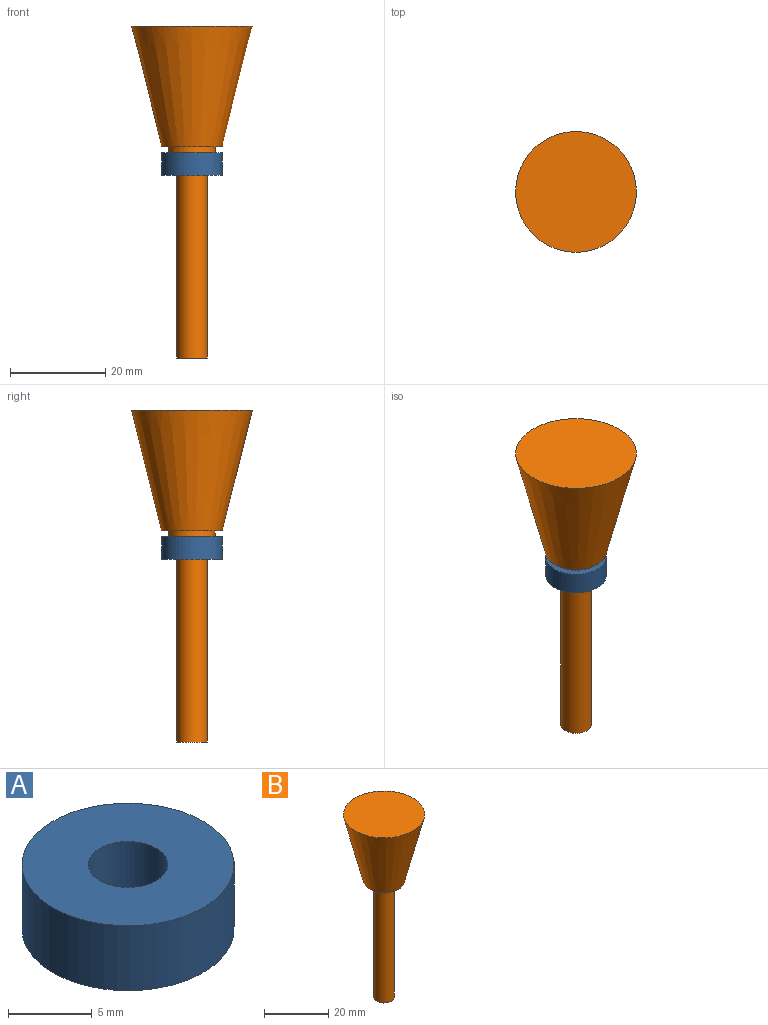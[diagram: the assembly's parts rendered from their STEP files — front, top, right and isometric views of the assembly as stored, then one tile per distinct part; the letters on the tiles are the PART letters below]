
ASSEMBLY  parts=2 mates=1
PART A: 4 faces, bbox 12.7x12.7x4.8 mm
  f0: cylinder r=2.38mm len=4.76mm, axis (0,0,-1), area 71.3mm2, adj f2,f3
  f1: cylinder r=6.35mm len=12.7mm, axis (0,0,-1), area 190mm2, adj f2,f3
  f2: plane 12.7x12.7mm, normal (0,0,1), area 108.9mm2, adj f0,f1
  f3: plane 12.7x12.7mm, normal (0,0,-1), area 108.9mm2, adj f0,f1
PART B: 7 faces, bbox 34.4x34.4x69.9 mm
  f0: torus R=42.94mm, axis (0,0,1), area 38.7mm2, adj f3,f4
  f1: plane 25.4x25.4mm, normal (0,0,1), area 506.7mm2, adj f2
  f2: cone r=12.7mm half-angle=14deg, axis (0,0,1), area 1568.1mm2, adj f1,f3
  f3: plane 12.73x12.73mm, normal (0,0,-1), area 53.7mm2, adj f0,f2
  f4: plane 9.73x9.73mm, normal (0,0,-1), area 42.7mm2, adj f0,f5
  f5: cylinder r=3.17mm len=43.18mm, axis (0,0,-1), area 861.4mm2, adj f4,f6
  f6: plane 6.35x6.35mm, normal (0,0,-1), area 31.7mm2, adj f5
PLACE A t=(-2.27,2.02,0.43)mm
PLACE B t=(-2.27,2.02,6.46)mm
MATE fastened A.f0 <-> B.f0  axis (0,0,1) through (-2.27,2.02,5.19)mm
